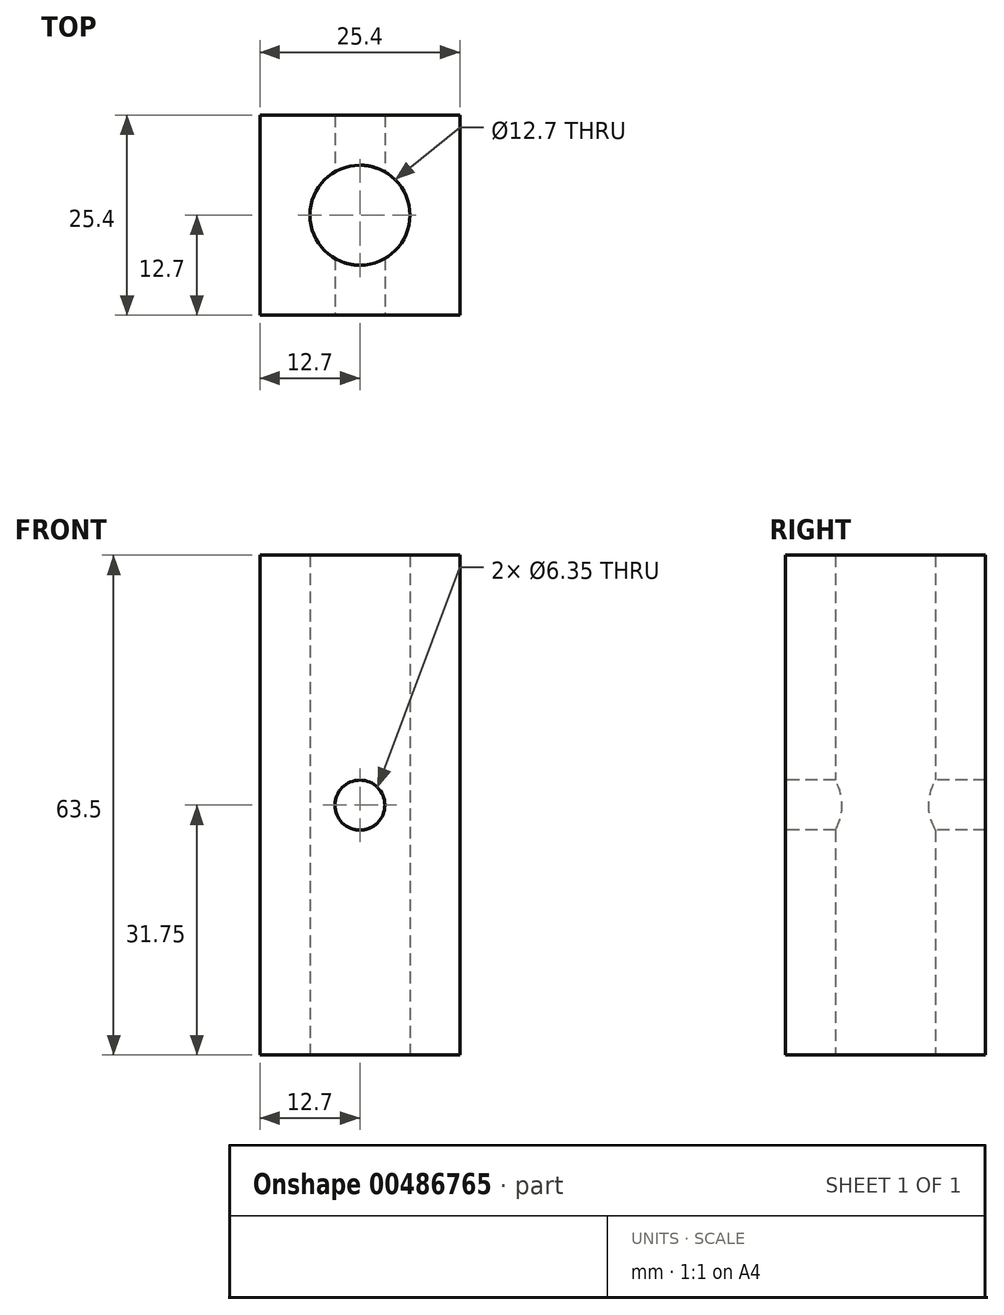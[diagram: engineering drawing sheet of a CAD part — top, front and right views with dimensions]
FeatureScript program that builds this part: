
annotation { "Feature Type Name" : "Feature", "Feature Type Description" : "" }
export const myFeature = defineFeature(function(context is Context, id is Id, definition is map)
    precondition{}
    {
        {
            var Q0;
            Q0=qCreatedBy(makeId("Top.planeOp"),FACE);
            var sketch = newSketch(context, id + "F0", { "sketchPlane" : qUnion([Q0])});
            skLineSegment(sketch, "E0.bottom", {"start": v(12.7, -12.7) * mm, "end": v(-12.7, -12.7) * mm});
            skLineSegment(sketch, "E0.top", {"start": v(12.7, 12.7) * mm, "end": v(-12.7, 12.7) * mm});
            skLineSegment(sketch, "E0.left", {"start": v(12.7, -12.7) * mm, "end": v(12.7, 12.7) * mm});
            skLineSegment(sketch, "E0.right", {"start": v(-12.7, -12.7) * mm, "end": v(-12.7, 12.7) * mm});
            skPoint(sketch, "E0.middle", {"position": v(0, 0) * mm});
            skCircle(sketch, "E1", {"center": v(0, 0) * mm, "radius": 6.35 * mm});
            skSolve(sketch);
        }
        {
            var Q0;
            Q0=makeQuery(id+"F0.imprint","IMPRINT",FACE,{"disambiguationData":[TD([[makeQuery(id+"F0.imprint","IMPRINT",EDGE,{"derivedFrom":sQuery(id+"F0.wireOp",EDGE,"E0.bottom")}),-1.0]])]});
            extrude(context, id + "F1", {"entities" : qUnion([Q0]), "depth" : 63.5 * mm});
        }
        {
            var Q0;
            Q0=makeQuery(id+"F1.opExtrude","SWEPT_FACE",FACE,{"disambiguationData":[OSD([sQuery(id+"F0.wireOp",EDGE,"E0.bottom")])]});
            var sketch = newSketch(context, id + "F2", { "sketchPlane" : qUnion([Q0])});
            skCircle(sketch, "E2", {"center": v(0, 31.75) * mm, "radius": 3.17 * mm});
            skSolve(sketch);
        }
        {
            var Q0;
            Q0 = qSketchRegion(id + "F2", true);
            extrude(context, id + "F3", {"entities" : qUnion([Q0]), "operationType" : NewBodyOperationType.REMOVE, "endBound" : BoundingType.THROUGH_ALL, "oppositeDirection" : true, "depth" : 25.4 * mm});
        }
    });
